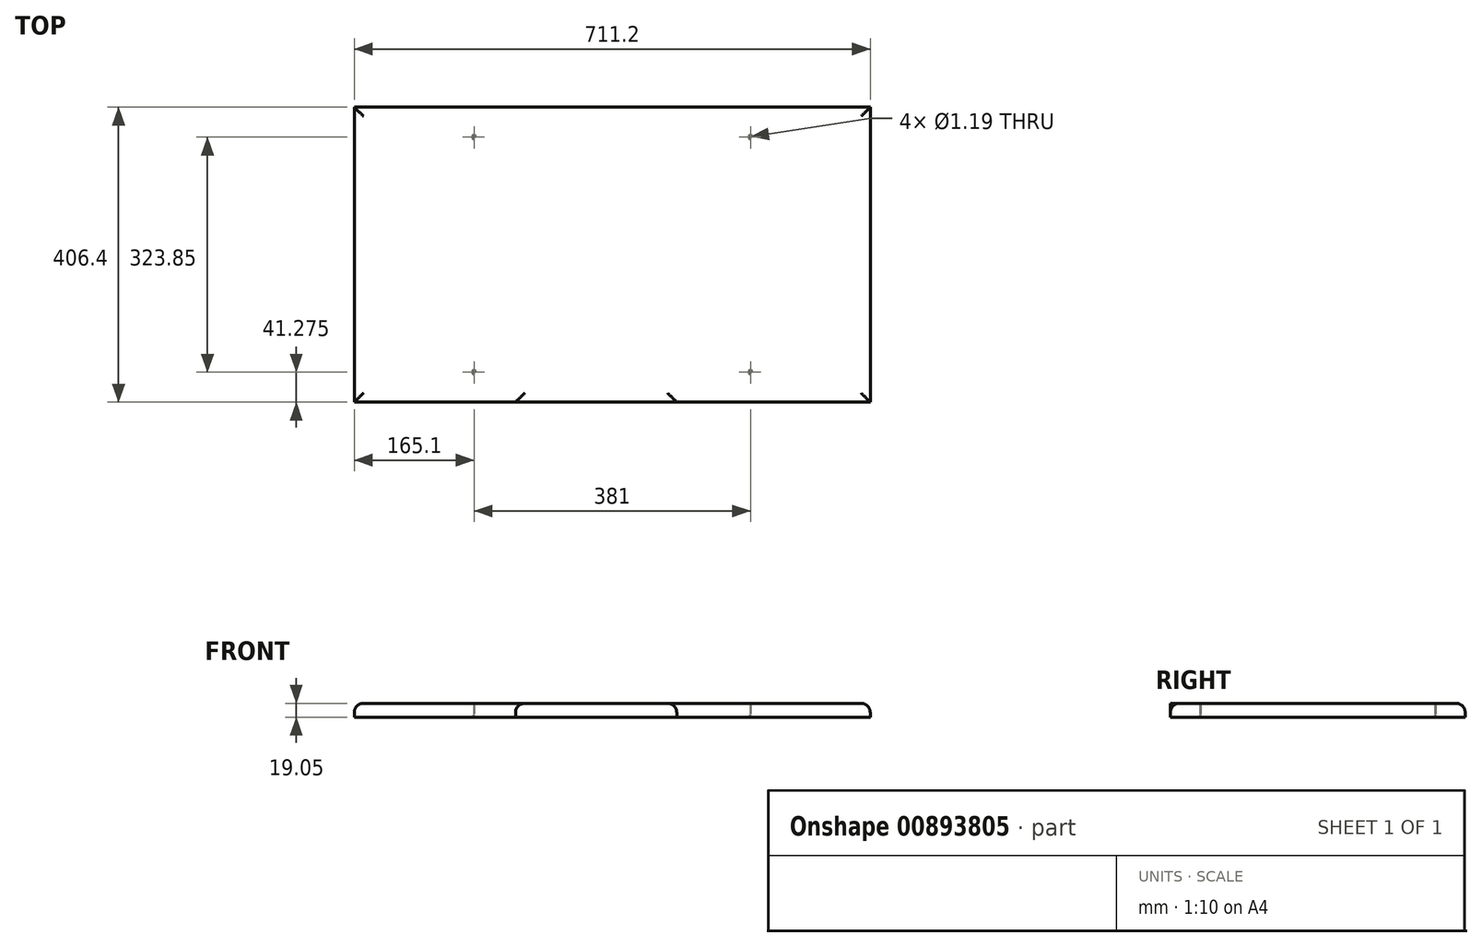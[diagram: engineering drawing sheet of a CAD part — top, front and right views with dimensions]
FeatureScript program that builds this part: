
annotation { "Feature Type Name" : "Feature", "Feature Type Description" : "" }
export const myFeature = defineFeature(function(context is Context, id is Id, definition is map)
    precondition{}
    {
        {
            var Q0;
            Q0=qCreatedBy(makeId("Top.planeOp"),FACE);
            var sketch = newSketch(context, id + "F0", { "sketchPlane" : qUnion([Q0])});
            skLineSegment(sketch, "E0.bottom", {"start": v(-355.6, -203.2) * mm, "end": v(355.6, -203.2) * mm});
            skLineSegment(sketch, "E0.top", {"start": v(-355.6, 203.2) * mm, "end": v(355.6, 203.2) * mm});
            skLineSegment(sketch, "E0.left", {"start": v(-355.6, -203.2) * mm, "end": v(-355.6, 203.2) * mm});
            skLineSegment(sketch, "E0.right", {"start": v(355.6, -203.2) * mm, "end": v(355.6, 203.2) * mm});
            skPoint(sketch, "E0.middle", {"position": v(0, 0) * mm});
            skSolve(sketch);
        }
        {
            var Q0;
            Q0=makeQuery(id+"F0.imprint","IMPRINT",FACE,{"disambiguationData":[TD([[makeQuery(id+"F0.imprint","IMPRINT",EDGE,{"derivedFrom":sQuery(id+"F0.wireOp",EDGE,"E0.bottom")}),1.0]])]});
            extrude(context, id + "F1", {"entities" : qUnion([Q0]), "depth" : 19.05 * mm, "offsetDistance" : 25.4 * mm});
        }
        {
            var Q0;
            Q0=makeQuery(id+"F1.opExtrude","SWEPT_FACE",FACE,{"disambiguationData":[OSD([sQuery(id+"F0.wireOp",EDGE,"E0.bottom")])]});
            var sketch = newSketch(context, id + "F2", { "sketchPlane" : qUnion([Q0])});
            skLineSegment(sketch, "E1.bottom", {"start": v(-133.35, 19.05) * mm, "end": v(88.9, 19.05) * mm});
            skLineSegment(sketch, "E1.top", {"start": v(-133.35, 0) * mm, "end": v(88.9, 0) * mm});
            skLineSegment(sketch, "E1.left", {"start": v(-133.35, 19.05) * mm, "end": v(-133.35, 0) * mm});
            skLineSegment(sketch, "E1.right", {"start": v(88.9, 19.05) * mm, "end": v(88.9, 0) * mm});
            skSolve(sketch);
        }
        {
            var Q0;
            Q0 = qSketchRegion(id + "F2", true);
            extrude(context, id + "F3", {"entities" : qUnion([Q0]), "operationType" : NewBodyOperationType.ADD, "depth" : 0 * mm, "offsetDistance" : 25.4 * mm});
        }
        {
            var Q0;
            {var subQ0=sQuery(id+"F0.wireOp",EDGE,"E0.left");var subQ1=sQuery(id+"F0.wireOp",EDGE,"E0.bottom");Q0=makeQuery(id+"F3.boolean.opBoolean","SPLIT",EDGE,{"disambiguationData":[TD([makeQuery(id+"F1.opExtrude","SWEPT_FACE",FACE,{"disambiguationData":[OSD([subQ0])]})])],"derivedFrom":makeQuery(id+"F1.opExtrude","CAP_EDGE",EDGE,{"disambiguationData":[OSD([subQ1])],"isStart":false})});}
            var Q1;
            Q1=makeQuery(id+"F1.opExtrude","CAP_EDGE",EDGE,{"disambiguationData":[OSD([sQuery(id+"F0.wireOp",EDGE,"E0.left")])],"isStart":false});
            var Q2;
            {var subQ0=sQuery(id+"F0.wireOp",EDGE,"E0.right");var subQ1=sQuery(id+"F0.wireOp",EDGE,"E0.bottom");Q2=makeQuery(id+"F3.boolean.opBoolean","SPLIT",EDGE,{"disambiguationData":[TD([makeQuery(id+"F1.opExtrude","SWEPT_FACE",FACE,{"disambiguationData":[OSD([subQ0])]})])],"derivedFrom":makeQuery(id+"F1.opExtrude","CAP_EDGE",EDGE,{"disambiguationData":[OSD([subQ1])],"isStart":false})});}
            var Q3;
            Q3=makeQuery(id+"F1.opExtrude","CAP_EDGE",EDGE,{"disambiguationData":[OSD([sQuery(id+"F0.wireOp",EDGE,"E0.right")])],"isStart":false});
            var Q4;
            Q4=makeQuery(id+"F1.opExtrude","CAP_EDGE",EDGE,{"disambiguationData":[OSD([sQuery(id+"F0.wireOp",EDGE,"E0.top")])],"isStart":false});
            fillet(context, id + "F4", {"entities" : qUnion([Q0, Q1, Q2, Q3, Q4]), "radius" : 12.7 * mm, "tangentPropagation" : true, "allowEdgeOverflow" : false});
        }
        {
            var Q0;
            Q0=makeQuery(id+"F3.opExtrude","SWEPT_EDGE",EDGE,{"disambiguationData":[OSD([sQuery(id+"F0.wireOp",EDGE,"E0.bottom"),sQuery(id+"F2.wireOp",EDGE,"E1.bottom"),sQuery(id+"F2.wireOp",EDGE,"E1.right")])]});
            var Q1;
            Q1=makeQuery(id+"F3.opExtrude","SWEPT_EDGE",EDGE,{"disambiguationData":[OSD([sQuery(id+"F0.wireOp",EDGE,"E0.bottom"),sQuery(id+"F2.wireOp",EDGE,"E1.bottom"),sQuery(id+"F2.wireOp",EDGE,"E1.left")])]});
            fillet(context, id + "F5", {"entities" : qUnion([Q0, Q1]), "radius" : 12.7 * mm, "tangentPropagation" : true, "allowEdgeOverflow" : false});
        }
        {
            var Q0;
            Q0=makeQuery(id+"F3.boolean.opBoolean","MERGE",FACE,{"derivedFrom":[makeQuery(id+"F1.opExtrude","CAP_FACE",FACE,{"disambiguationData":[OSD([sQuery(id+"F0.wireOp",EDGE,"E0.bottom"),sQuery(id+"F0.wireOp",EDGE,"E0.top"),sQuery(id+"F0.wireOp",EDGE,"E0.left"),sQuery(id+"F0.wireOp",EDGE,"E0.right")])],"isStart":true}),makeQuery(id+"F3.opExtrude","SWEPT_FACE",FACE,{"disambiguationData":[OSD([sQuery(id+"F2.wireOp",EDGE,"E1.top")])]})]});
            var sketch = newSketch(context, id + "F6", { "sketchPlane" : qUnion([Q0])});
            skPoint(sketch, "E2", {"position": v(190.5, -161.92) * mm});
            skPoint(sketch, "E3", {"position": v(190.5, 161.92) * mm});
            skPoint(sketch, "E4", {"position": v(-190.5, 161.92) * mm});
            skPoint(sketch, "E5", {"position": v(-190.5, -161.93) * mm});
            skSolve(sketch);
        }
        {
            var Q0;
            Q0=sQuery(id+"F6.wireOp",VERTEX,"E2");
            var Q1;
            Q1=sQuery(id+"F6.wireOp",VERTEX,"E3");
            var Q2;
            Q2=sQuery(id+"F6.wireOp",VERTEX,"E5");
            var Q3;
            Q3=sQuery(id+"F6.wireOp",VERTEX,"E4");
            var Q4;
            Q4=makeQuery(id+"F1.opExtrude","SWEPT_BODY",BODY,{"disambiguationData":[OSD([sQuery(id+"F0.wireOp",EDGE,"E0.bottom"),sQuery(id+"F0.wireOp",EDGE,"E0.top"),sQuery(id+"F0.wireOp",EDGE,"E0.left"),sQuery(id+"F0.wireOp",EDGE,"E0.right")])]});
            hole(context, id + "F7", {"style" : HoleStyle.C_SINK, "endStyle" : HoleEndStyle.THROUGH, "holeDiameter" : 1.2 * mm, "cSinkDiameter" : 6.35 * mm, "cSinkAngle" : 90 * degree, "majorDiameter" : 6.35 * mm, "isTappedThrough" : true, "tappedDepth" : 12.7 * mm, "tapClearance" : 3, "locations" : qUnion([Q0, Q1, Q2, Q3]), "scope" : qUnion([Q4])});
        }
    });
